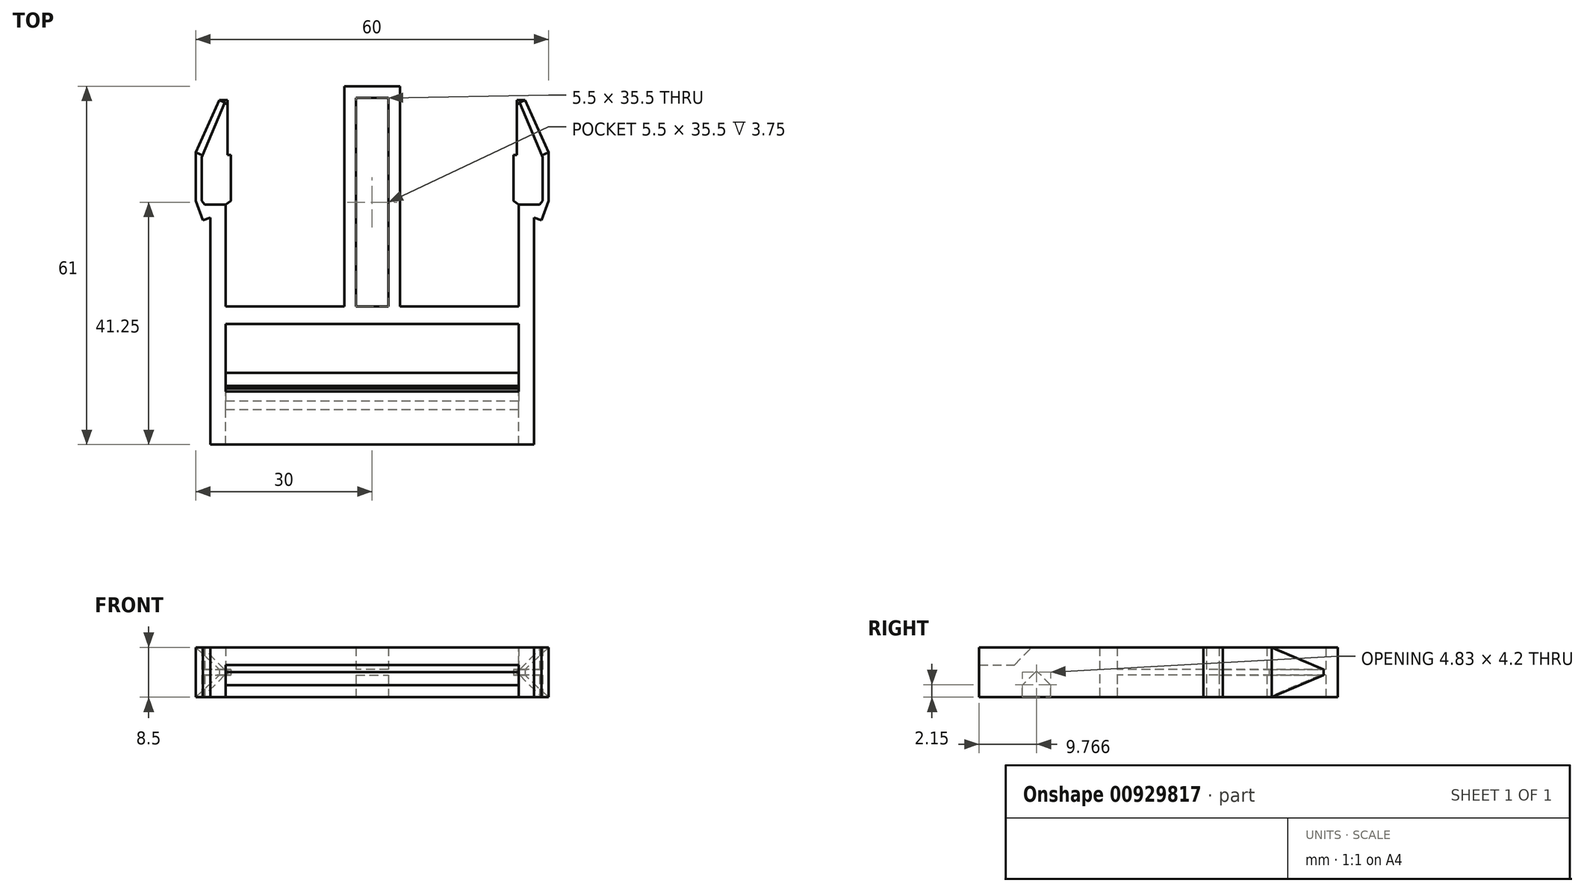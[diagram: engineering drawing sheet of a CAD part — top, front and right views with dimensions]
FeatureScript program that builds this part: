
annotation { "Feature Type Name" : "Feature", "Feature Type Description" : "" }
export const myFeature = defineFeature(function(context is Context, id is Id, definition is map)
    precondition{}
    {
        {
            var Q0;
            Q0=qCreatedBy(makeId("Top.planeOp"),FACE);
            var sketch = newSketch(context, id + "F0", { "sketchPlane" : qUnion([Q0])});
            skLineSegment(sketch, "E0.bottom", {"start": v(0, 0) * mm, "end": v(4.75, 0) * mm});
            skLineSegment(sketch, "E0.top", {"start": v(0, 37.5) * mm, "end": v(4.75, 37.5) * mm});
            skLineSegment(sketch, "E0.left", {"start": v(0, 0) * mm, "end": v(0, 37.5) * mm});
            skLineSegment(sketch, "E0.right", {"start": v(4.75, 0) * mm, "end": v(4.75, 37.5) * mm});
            skLineSegment(sketch, "E1", {"start": v(2.75, 35.5) * mm, "end": v(2.75, 0) * mm});
            skLineSegment(sketch, "E2", {"start": v(2.75, 35.5) * mm, "end": v(0, 35.5) * mm});
            skLineSegment(sketch, "E3.bottom", {"start": v(0, 0) * mm, "end": v(27.5, 0) * mm});
            skLineSegment(sketch, "E3.top", {"start": v(0, -3) * mm, "end": v(27.5, -3) * mm});
            skLineSegment(sketch, "E3.left", {"start": v(0, 0) * mm, "end": v(0, -3) * mm});
            skLineSegment(sketch, "E3.right", {"start": v(27.5, 0) * mm, "end": v(27.5, -3) * mm});
            skLineSegment(sketch, "E4.bottom", {"start": v(27.5, 0) * mm, "end": v(24.9, 0) * mm});
            skLineSegment(sketch, "E4.top", {"start": v(27.5, 15.6) * mm, "end": v(24.9, 15.6) * mm});
            skLineSegment(sketch, "E4.left", {"start": v(27.5, 0) * mm, "end": v(27.5, 15.6) * mm});
            skLineSegment(sketch, "E4.right", {"start": v(24.9, 0) * mm, "end": v(24.9, 15.6) * mm});
            skLineSegment(sketch, "E5.bottom", {"start": v(27.5, -3) * mm, "end": v(24.9, -3) * mm});
            skLineSegment(sketch, "E5.top", {"start": v(27.5, -23.5) * mm, "end": v(24.9, -23.5) * mm});
            skLineSegment(sketch, "E5.left", {"start": v(27.5, -3) * mm, "end": v(27.5, -23.5) * mm});
            skLineSegment(sketch, "E5.right", {"start": v(24.9, -3) * mm, "end": v(24.9, -23.5) * mm});
            skLineSegment(sketch, "E6.bottom", {"start": v(24.9, -13.25) * mm, "end": v(0, -13.25) * mm});
            skLineSegment(sketch, "E6.top", {"start": v(24.9, -16.25) * mm, "end": v(0, -16.25) * mm});
            skLineSegment(sketch, "E6.left", {"start": v(24.9, -13.25) * mm, "end": v(24.9, -16.25) * mm});
            skLineSegment(sketch, "E6.right", {"start": v(0, -13.25) * mm, "end": v(0, -16.25) * mm});
            skLineSegment(sketch, "E7.bottom", {"start": v(24.9, 15.6) * mm, "end": v(30, 15.6) * mm});
            skLineSegment(sketch, "E7.top", {"start": v(24.9, 37.5) * mm, "end": v(30, 37.5) * mm});
            skLineSegment(sketch, "E7.left", {"start": v(24.9, 15.6) * mm, "end": v(24.9, 37.5) * mm});
            skLineSegment(sketch, "E7.right", {"start": v(30, 15.6) * mm, "end": v(30, 37.5) * mm});
            skLineSegment(sketch, "E8", {"start": v(29.16, 15.6) * mm, "end": v(30, 17.97) * mm});
            skLineSegment(sketch, "E9", {"start": v(30, 26.25) * mm, "end": v(24.9, 37.5) * mm});
            skLineSegment(sketch, "E10", {"start": v(24.9, 17.32) * mm, "end": v(28.5, 17.32) * mm});
            skLineSegment(sketch, "E11", {"start": v(28.5, 17.32) * mm, "end": v(29, 17.97) * mm});
            skLineSegment(sketch, "E12", {"start": v(29, 17.97) * mm, "end": v(29, 25.42) * mm});
            skLineSegment(sketch, "E13", {"start": v(29, 25.42) * mm, "end": v(24.9, 35.11) * mm});
            skLineSegment(sketch, "E14", {"start": v(24.9, 35.11) * mm, "end": v(25.98, 35.11) * mm});
            skLineSegment(sketch, "E15", {"start": v(25.98, 35.11) * mm, "end": v(30, 35.11) * mm});
            skLineSegment(sketch, "E16", {"start": v(24.9, 17.32) * mm, "end": v(24.06, 17.97) * mm});
            skLineSegment(sketch, "E17", {"start": v(24.06, 17.97) * mm, "end": v(24.06, 25.8) * mm});
            skLineSegment(sketch, "E18", {"start": v(24.06, 25.8) * mm, "end": v(24.58, 25.8) * mm});
            skLineSegment(sketch, "E19", {"start": v(24.58, 25.8) * mm, "end": v(24.58, 35.11) * mm});
            skLineSegment(sketch, "E20", {"start": v(24.9, 35.11) * mm, "end": v(24.58, 35.11) * mm});
            skLineSegment(sketch, "E21.bottom", {"start": v(0, -13.25) * mm, "end": v(24.9, -13.25) * mm});
            skLineSegment(sketch, "E21.top", {"start": v(0, -11.22) * mm, "end": v(24.9, -11.22) * mm});
            skLineSegment(sketch, "E21.left", {"start": v(0, -13.25) * mm, "end": v(0, -11.22) * mm});
            skLineSegment(sketch, "E21.right", {"start": v(24.9, -13.25) * mm, "end": v(24.9, -11.22) * mm});
            skLineSegment(sketch, "E22", {"start": v(29.16, 15.6) * mm, "end": v(28.83, 14.66) * mm});
            skLineSegment(sketch, "E23", {"start": v(28.83, 14.66) * mm, "end": v(27.5, 15.13) * mm});
            skSolve(sketch);
        }
        {
            var Q0;
            {var subQ3=sQuery(id+"F0.wireOp",EDGE,"E1");Q0=makeQuery(id+"F0.imprint","IMPRINT",FACE,{"disambiguationData":[TD([[makeQuery(id+"F0.imprint","IMPRINT",EDGE,{"derivedFrom":subQ3}),-1.0]])]});}
            var Q1;
            {var subQ0=sQuery(id+"F0.wireOp",EDGE,"E10");Q1=makeQuery(id+"F0.imprint","IMPRINT",FACE,{"disambiguationData":[TD([[makeQuery(id+"F0.imprint","IMPRINT",EDGE,{"derivedFrom":subQ0}),1.0]])]});}
            var Q2;
            {var subQ0=sQuery(id+"F0.wireOp",EDGE,"E16");Q2=makeQuery(id+"F0.imprint","IMPRINT",FACE,{"disambiguationData":[TD([[makeQuery(id+"F0.imprint","IMPRINT",EDGE,{"derivedFrom":subQ0}),-1.0]])]});}
            extrude(context, id + "F1", {"entities" : qUnion([Q0, Q1, Q2]), "endBound" : BoundingType.SYMMETRIC, "depth" : 1 * mm, "offsetDistance" : 25 * mm});
        }
        {
            var Q0;
            {var subQ2=sQuery(id+"F0.wireOp",EDGE,"E0.top");Q0=makeQuery(id+"F0.imprint","IMPRINT",FACE,{"disambiguationData":[TD([[makeQuery(id+"F0.imprint","IMPRINT",EDGE,{"derivedFrom":subQ2}),-1.0]])]});}
            var Q1;
            {var subQ6=sQuery(id+"F0.wireOp",EDGE,"E3.left");Q1=makeQuery(id+"F0.imprint","IMPRINT",FACE,{"disambiguationData":[TD([[makeQuery(id+"F0.imprint","IMPRINT",EDGE,{"derivedFrom":subQ6}),1.0]])]});}
            var Q2;
            {var subQ1=sQuery(id+"F0.wireOp",EDGE,"E4.top");Q2=makeQuery(id+"F0.imprint","IMPRINT",FACE,{"disambiguationData":[TD([[makeQuery(id+"F0.imprint","IMPRINT",EDGE,{"derivedFrom":subQ1}),1.0]])]});}
            var Q3;
            {var subQ5=sQuery(id+"F0.wireOp",EDGE,"E5.top");Q3=makeQuery(id+"F0.imprint","IMPRINT",FACE,{"disambiguationData":[TD([[makeQuery(id+"F0.imprint","IMPRINT",EDGE,{"derivedFrom":subQ5}),-1.0]])]});}
            var Q4;
            {var subQ2=sQuery(id+"F0.wireOp",EDGE,"E4.top");Q4=makeQuery(id+"F0.imprint","IMPRINT",FACE,{"disambiguationData":[TD([[makeQuery(id+"F0.imprint","IMPRINT",EDGE,{"derivedFrom":subQ2}),-1.0]])]});}
            var Q5;
            {var subQ4=sQuery(id+"F0.wireOp",EDGE,"E22");Q5=makeQuery(id+"F0.imprint","IMPRINT",FACE,{"disambiguationData":[TD([[makeQuery(id+"F0.imprint","IMPRINT",EDGE,{"derivedFrom":subQ4}),-1.0]])]});}
            extrude(context, id + "F2", {"entities" : qUnion([Q0, Q1, Q2, Q3, Q4, Q5]), "operationType" : NewBodyOperationType.ADD, "endBound" : BoundingType.SYMMETRIC, "depth" : 8.5 * mm, "offsetDistance" : 25 * mm});
        }
        {
            var Q0;
            {var subQ0=sQuery(id+"F0.wireOp",EDGE,"E6.bottom");Q0=makeQuery(id+"F0.imprint","IMPRINT",FACE,{"disambiguationData":[TD([[makeQuery(id+"F0.imprint","IMPRINT",EDGE,{"derivedFrom":subQ0}),1.0]])]});}
            var Q1;
            {var subQ0=sQuery(id+"F0.wireOp",EDGE,"E6.bottom");Q1=makeQuery(id+"F0.imprint","IMPRINT",FACE,{"disambiguationData":[TD([[makeQuery(id+"F0.imprint","IMPRINT",EDGE,{"derivedFrom":subQ0}),-1.0]])]});}
            extrude(context, id + "F3", {"entities" : qUnion([Q0, Q1]), "operationType" : NewBodyOperationType.ADD, "oppositeDirection" : true, "depth" : 2.2 * mm, "offsetDistance" : 25 * mm});
        }
        {
            var Q0;
            Q0=makeQuery(id+"F3.opExtrude","CAP_EDGE",EDGE,{"disambiguationData":[OSD([sQuery(id+"F0.wireOp",EDGE,"E6.top")])],"isStart":true});
            var Q1;
            Q1=makeQuery(id+"F3.opExtrude","CAP_EDGE",EDGE,{"disambiguationData":[OSD([sQuery(id+"F0.wireOp",EDGE,"E21.top")])],"isStart":true});
            chamfer(context, id + "F4", {"entities" : qUnion([Q0, Q1]), "width" : 2.3 * mm, "tangentPropagation" : true});
        }
        {
            var Q0;
            Q0=makeQuery(id+"F2.opExtrude","SWEPT_FACE",FACE,{"disambiguationData":[OSD([sQuery(id+"F0.wireOp",EDGE,"E5.right")])]});
            var sketch = newSketch(context, id + "F5", { "sketchPlane" : qUnion([Q0])});
            skLineSegment(sketch, "E24.bottom", {"start": v(23.5, 4.25) * mm, "end": v(14.5, 4.25) * mm});
            skLineSegment(sketch, "E24.top", {"start": v(23.5, 1.25) * mm, "end": v(14.5, 1.25) * mm});
            skLineSegment(sketch, "E24.left", {"start": v(23.5, 4.25) * mm, "end": v(23.5, 1.25) * mm});
            skLineSegment(sketch, "E24.right", {"start": v(14.5, 4.25) * mm, "end": v(14.5, 1.25) * mm});
            skSolve(sketch);
        }
        {
            var Q0;
            Q0 = qSketchRegion(id + "F5", true);
            extrude(context, id + "F6", {"entities" : qUnion([Q0]), "operationType" : NewBodyOperationType.ADD, "depth" : 25 * mm, "offsetDistance" : 25 * mm});
        }
        {
            var Q0;
            Q0=makeQuery(id+"F6.opExtrude","SWEPT_EDGE",EDGE,{"disambiguationData":[OSD([sQuery(id+"F5.wireOp",EDGE,"E24.top"),sQuery(id+"F5.wireOp",EDGE,"E24.right")])]});
            chamfer(context, id + "F7", {"entities" : qUnion([Q0]), "width" : 3 * mm, "tangentPropagation" : true});
        }
        {
            var Q0;
            Q0=makeQuery(id+"F3.opExtrude","CAP_FACE",FACE,{"disambiguationData":[OSD([sQuery(id+"F0.wireOp",EDGE,"E5.right"),sQuery(id+"F0.wireOp",EDGE,"E6.top"),sQuery(id+"F0.wireOp",EDGE,"E6.right"),sQuery(id+"F0.wireOp",EDGE,"E21.top"),sQuery(id+"F0.wireOp",EDGE,"E21.left")])],"isStart":false});
            extrude(context, id + "F8", {"entities" : qUnion([Q0]), "operationType" : NewBodyOperationType.ADD, "depth" : 2 * mm, "offsetDistance" : 25 * mm});
        }
        {
            var Q0;
            Q0=makeQuery(id+"F2.opExtrude","SWEPT_FACE",FACE,{"disambiguationData":[OSD([sQuery(id+"F0.wireOp",EDGE,"E9")])]});
            var sketch = newSketch(context, id + "F9", { "sketchPlane" : qUnion([Q0])});
            skLineSegment(sketch, "E25", {"start": v(11.52, 4.25) * mm, "end": v(21.25, 0.47) * mm});
            skLineSegment(sketch, "E26", {"start": v(11.52, -4.25) * mm, "end": v(21.25, -0.48) * mm});
            skSolve(sketch);
        }
        {
            var Q0;
            {var subQ0=sQuery(id+"F9.wireOp",EDGE,"E25");Q0=makeQuery(id+"F9.imprint","IMPRINT",FACE,{"disambiguationData":[TD([[makeQuery(id+"F9.imprint","IMPRINT",EDGE,{"derivedFrom":subQ0}),1.0]])]});}
            var Q1;
            {var subQ0=sQuery(id+"F9.wireOp",EDGE,"E26");Q1=makeQuery(id+"F9.imprint","IMPRINT",FACE,{"disambiguationData":[TD([[makeQuery(id+"F9.imprint","IMPRINT",EDGE,{"derivedFrom":subQ0}),-1.0]])]});}
            extrude(context, id + "F10", {"entities" : qUnion([Q0, Q1]), "operationType" : NewBodyOperationType.REMOVE, "oppositeDirection" : true, "depth" : 15 * mm, "offsetDistance" : 25 * mm});
        }
        {
            var Q0;
            {var subQ0=sQuery(id+"F0.wireOp",EDGE,"E9");var subQ1=sQuery(id+"F0.wireOp",EDGE,"E15");var subQ2=sQuery(id+"F0.wireOp",EDGE,"E14");var subQ3=makeQuery(id+"F2.opExtrude","SWEPT_EDGE",EDGE,{"disambiguationData":[OSD([subQ0,subQ2,subQ1])]});Q0=makeQuery(id+"F10.boolean.opBoolean","COPY",FACE,{"derivedFrom":makeQuery(id+"F10.opExtrude","SWEPT_FACE",FACE,{"disambiguationData":[OSD([subQ0,subQ2,subQ1]),TDD([makeQuery(id+"F9.imprint","IMPRINT",EDGE,{"disambiguationData":[TD([[makeQuery(id+"F9.imprint","INTERSECT",VERTEX,{"derivedFrom":[subQ3,makeQuery(id+"F2.opExtrude","CAP_EDGE",EDGE,{"disambiguationData":[OSD([subQ0])],"isStart":false})]}),-1.0]])],"derivedFrom":subQ3})])]})});}
            var Q1;
            {var subQ0=sQuery(id+"F0.wireOp",EDGE,"E9");var subQ1=sQuery(id+"F0.wireOp",EDGE,"E15");var subQ2=sQuery(id+"F0.wireOp",EDGE,"E14");var subQ3=makeQuery(id+"F2.opExtrude","SWEPT_EDGE",EDGE,{"disambiguationData":[OSD([subQ0,subQ2,subQ1])]});Q1=makeQuery(id+"F10.boolean.opBoolean","COPY",FACE,{"derivedFrom":makeQuery(id+"F10.opExtrude","SWEPT_FACE",FACE,{"disambiguationData":[OSD([subQ0,subQ2,subQ1]),TDD([makeQuery(id+"F9.imprint","IMPRINT",EDGE,{"disambiguationData":[TD([[makeQuery(id+"F9.imprint","INTERSECT",VERTEX,{"derivedFrom":[subQ3,makeQuery(id+"F2.opExtrude","CAP_EDGE",EDGE,{"disambiguationData":[OSD([subQ0])],"isStart":true})]}),1.0]])],"derivedFrom":subQ3})])]})});}
            extrude(context, id + "F11", {"entities" : qUnion([Q0, Q1]), "operationType" : NewBodyOperationType.REMOVE, "oppositeDirection" : true, "depth" : 25 * mm, "offsetDistance" : 25 * mm});
        }
        {
            var Q0;
            Q0=makeQuery(id+"F1.opExtrude","SWEPT_BODY",BODY,{"disambiguationData":[OSD([sQuery(id+"F0.wireOp",EDGE,"E0.bottom"),sQuery(id+"F0.wireOp",EDGE,"E0.left"),sQuery(id+"F0.wireOp",EDGE,"E1"),sQuery(id+"F0.wireOp",EDGE,"E2")])]});
            var Q1;
            Q1=makeQuery(id+"F1.opExtrude","SWEPT_BODY",BODY,{"disambiguationData":[OSD([sQuery(id+"F0.wireOp",EDGE,"E10"),sQuery(id+"F0.wireOp",EDGE,"E11"),sQuery(id+"F0.wireOp",EDGE,"E12"),sQuery(id+"F0.wireOp",EDGE,"E13"),sQuery(id+"F0.wireOp",EDGE,"E16"),sQuery(id+"F0.wireOp",EDGE,"E17"),sQuery(id+"F0.wireOp",EDGE,"E18"),sQuery(id+"F0.wireOp",EDGE,"E19"),sQuery(id+"F0.wireOp",EDGE,"E20")])]});
            var Q2;
            Q2=qCreatedBy(makeId("Right.planeOp"),FACE);
            mirror(context, id + "F12", {"operationType" : NewBodyOperationType.ADD, "entities" : qUnion([Q0, Q1]), "mirrorPlane" : qUnion([Q2])});
        }
    });
